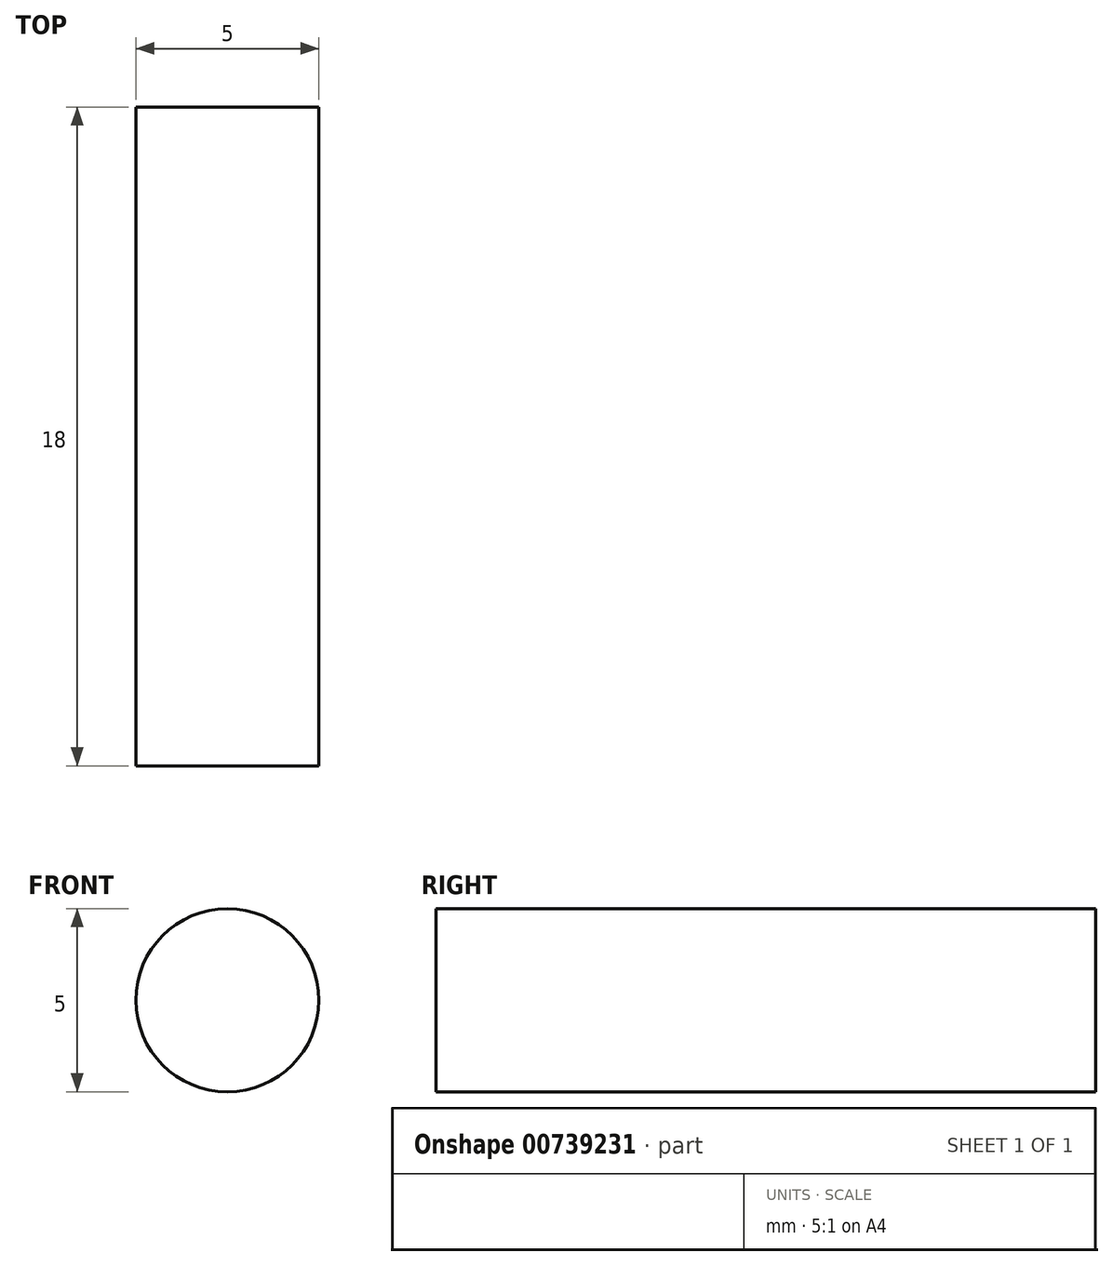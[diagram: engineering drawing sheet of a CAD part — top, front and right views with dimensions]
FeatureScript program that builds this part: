
annotation { "Feature Type Name" : "Feature", "Feature Type Description" : "" }
export const myFeature = defineFeature(function(context is Context, id is Id, definition is map)
    precondition{}
    {
        {
            var Q0;
            Q0=qCreatedBy(makeId("Front.planeOp"),FACE);
            var sketch = newSketch(context, id + "F0", { "sketchPlane" : qUnion([Q0])});
            skCircle(sketch, "E0", {"center": v(0, 0) * mm, "radius": 2.5 * mm});
            skSolve(sketch);
        }
        {
            var Q0;
            Q0 = qSketchRegion(id + "F0", true);
            extrude(context, id + "F1", {"entities" : qUnion([Q0]), "depth" : 18 * mm, "offsetDistance" : 25.4 * mm});
        }
    });
